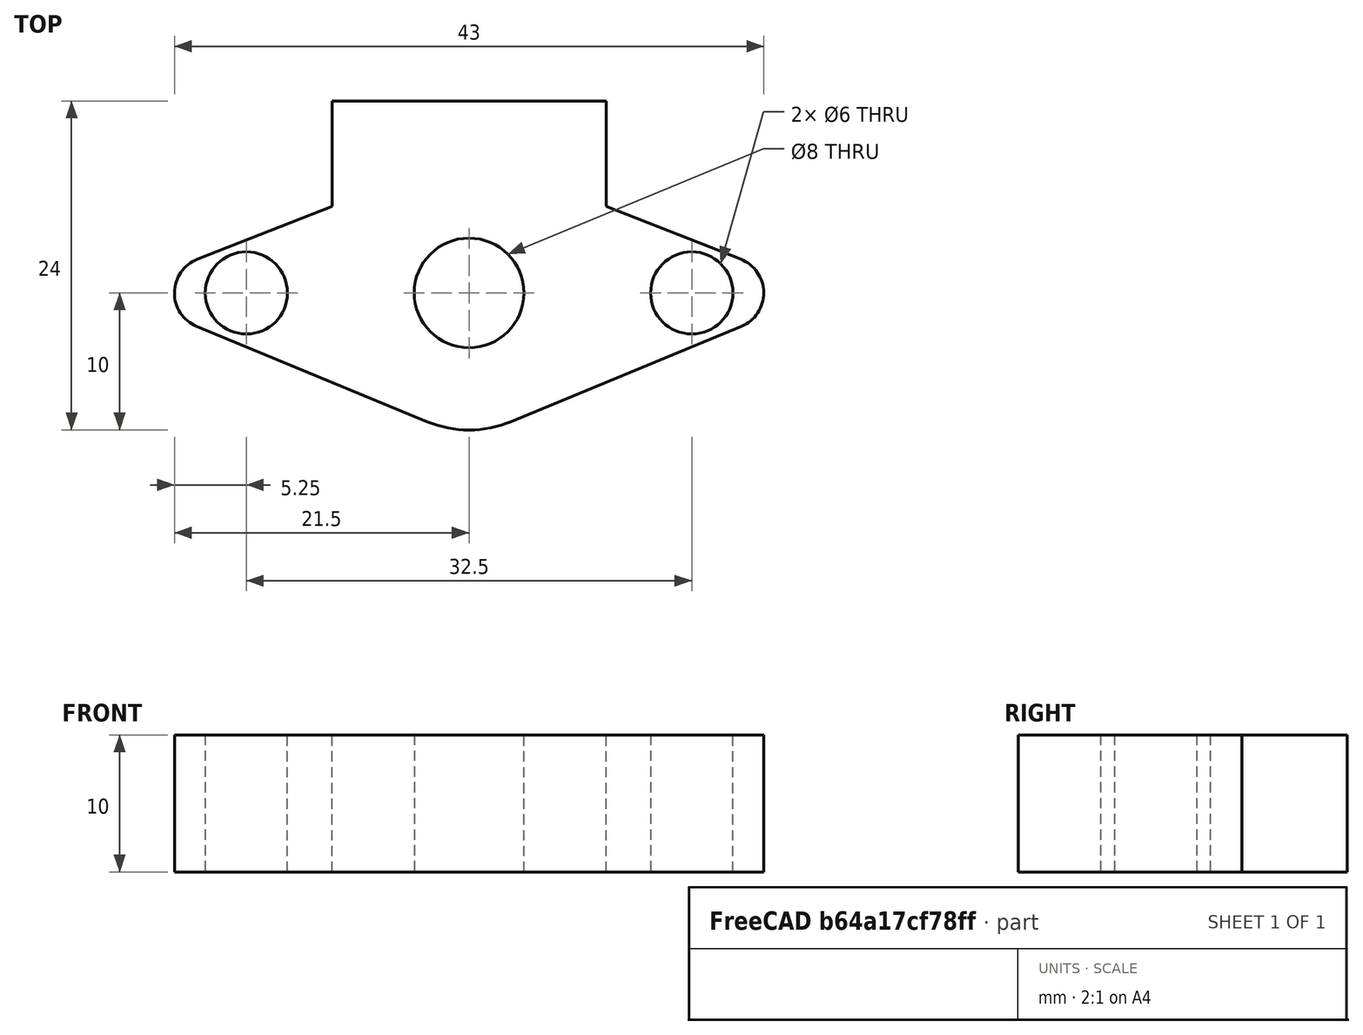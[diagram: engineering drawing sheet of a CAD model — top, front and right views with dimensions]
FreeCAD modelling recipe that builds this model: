
FCSTD DOCUMENT  (FreeCAD 0.16R6706 (Git))
Label: Suporte horizontal haste 8mm
License: All rights reserved
LicenseURL: http://en.wikipedia.org/wiki/All_rights_reserved
objects: Drawing::FeatureViewPython×5, Drawing::FeatureViewPart×2, Sketcher::SketchObject×1, PartDesign::Pad×1, Drawing::FeaturePage×1
note: 3 computed .brp shape members not serialized (recipe doc carries the construction recipe); baked Part::Feature solids carry a one-line shape summary decoded from their .brp

FEATURE [Sketcher::SketchObject] Sketch
  sketch-geometry (15):
    g0: LineSegment [constr] StartX=0 StartY=10 StartZ=0 EndX=0 EndY=-10 EndZ=0
    g1: LineSegment [constr] StartX=-21.5 StartY=0 StartZ=0 EndX=21.5 EndY=0 EndZ=0
    g2: LineSegment StartX=-19.8183 StartY=2.46551 StartZ=0 EndX=-10 EndY=6.31403 EndZ=0
    g3: LineSegment StartX=10 StartY=6.31403 StartZ=0 EndX=19.8183 EndY=2.46551 EndZ=0
    g4: LineSegment StartX=19.8633 StartY=-2.44736 StartZ=0 EndX=3.0585 EndY=-9.39286 EndZ=0
    g5: LineSegment StartX=-3.0585 StartY=-9.39286 StartZ=0 EndX=-19.8633 EndY=-2.44736 EndZ=0
    g6: ArcOfCircle CenterX=-18.8518 CenterY=0 CenterZ=0 NormalX=0 NormalY=0 NormalZ=1 Radius=2.64815 StartAngle=1.94437 EndAngle=4.32047
    g7: ArcOfCircle CenterX=18.8518 CenterY=0 CenterZ=0 NormalX=0 NormalY=0 NormalZ=1 Radius=2.64815 StartAngle=5.10431 EndAngle=7.48041
    g8: ArcOfCircle CenterX=0 CenterY=-1.99273 CenterZ=0 NormalX=0 NormalY=0 NormalZ=1 Radius=8.00727 StartAngle=4.32047 EndAngle=5.10431
    g9: Circle CenterX=0 CenterY=0 CenterZ=0 NormalX=0 NormalY=0 NormalZ=1 Radius=4
    g10: Circle CenterX=-16.25 CenterY=0 CenterZ=0 NormalX=0 NormalY=0 NormalZ=1 Radius=3
    g11: Circle CenterX=16.25 CenterY=0 CenterZ=0 NormalX=0 NormalY=0 NormalZ=1 Radius=3
    g12: LineSegment StartX=-10 StartY=14 StartZ=0 EndX=10 EndY=14 EndZ=0
    g13: LineSegment StartX=10 StartY=14 StartZ=0 EndX=10 EndY=6.31403 EndZ=0
    g14: LineSegment StartX=-10 StartY=6.31403 StartZ=0 EndX=-10 EndY=14 EndZ=0
  constraints (36):
    c: Vertical(g0)
    c: Horizontal(g1)
    c: Symmetric(g0,g0,g-1)
    c: Symmetric(g1,g1,g-1)
    c: Tangent(g2,g6) = 1.5708
    c: Tangent(g5,g6) = 1.5708
    c: Tangent(g3,g7) = 1.5708
    c: Tangent(g4,g7) = 1.5708
    c: Tangent(g4,g8) = 1.5708
    c: Tangent(g5,g8) = 1.5708
    c: PointOnObject(g7,g1)
    c: PointOnObject(g8,g0)
    c: PointOnObject(g6,g1)
    c: PointOnObject(g1,g6)
    c: PointOnObject(g1,g7)
    c: PointOnObject(g0,g8)
    c: DistanceY(g0,g0) = 20
    c: DistanceX(g1,g1) = 43
    c: Equal(g6,g7)
    c: PointOnObject(g11,g1)
    c: PointOnObject(g10,g1)
    c: Symmetric(g10,g11,g-1)
    c: Radius(g10) = 3
    c: Equal(g10,g11)
    c: Coincident(g9,g-1)
    c: Radius(g9) = 4
    c: DistanceX(g10,g11) = 32.5
    c: Coincident(g12,g13)
    c: Coincident(g14,g12)
    c: Horizontal(g12)
    c: Vertical(g13)
    c: Vertical(g14)
    c: Symmetric(g12,g12,g-2)
    c: DistanceX(g12,g12) = 20
    c: Coincident(g3,g13)
    c: Coincident(g2,g14)
FEATURE [PartDesign::Pad] Pad
  Length = 10
  Length2 = 100
  Sketch = -> Sketch
  Type = 0
FEATURE [Drawing::FeatureViewPart] Ortho  label="Ortho_0_0"
  Direction = (1,0,0)
  HiddenWidth = 0.15
  LineWidth = 0.35
  Rotation = -90
  Scale = 4
  ShowHiddenLines = true
  ShowSmoothLines = false
  Source = -> Pad
  Tolerance = 0.05
  ViewResult = <blob: 7028 chars omitted>
  Visible = true
  X = 97
  Y = 268.613
FEATURE [Drawing::FeatureViewPart] Ortho004  label="Ortho_0_1"
  Direction = (0,0,1)
  HiddenWidth = 0.15
  LineWidth = 0.35
  Rotation = 90
  Scale = 4
  ShowHiddenLines = true
  ShowSmoothLines = false
  Source = -> Pad
  Tolerance = 0.05
  ViewResult = <g id="Ortho_0_1"\n   transform="rotate(90,97,114.307) translate(97,114.307) scale(4,4)"\n  >\n<g   stroke="rgb(0, 0, 0)"\n   stroke-width="0.0375"\n   stroke-linecap="butt"\n   stroke-linejoin="miter"\n   stroke-dasharray="0.2,0.1"\n   fill="none"\n   transform="scale(1,-1)"\n  >\n<path id= "1" d=" M -3.0585 -9.39286 L -19.8633 -2.44736 " />\n<path d="M-19.8183 2.46551 A2.64815 2.64815 0 0 1 -19.8633 -2.44736" /><path id= "3" d=" M -19.8183 2.46551 L -10 6.31403 " />\n<path id= "4" d=" M -10 6.31403 L -10 14 " />\n<path id= "5" d=" M -10 14 L 10 14 " />\n<path id= "6" d=" M 10 14 L 10 6.31403 " />\n<path id= "7" d=" M 10 6.31403 L 19.8183 2.46551 " />\n<path d="M19.8633 -2.44736 A2.64815 2.64815 0 0 1 19.8183 2.46551" /><path id= "9" d=" M 19.8633 -2.44736 L 3.0585 -9.39286 " />\n<path d="M-3.0585 -9.39286 A8.00727 8.00727 0 0 1 3.0585 -9.39286" /><circle cx ="0" cy ="0" r ="4" /><circle cx ="16.25" cy ="0" r ="3" /><circle cx ="-16.25" cy ="0" r ="3" /></g>\n<g   stroke="rgb(0, 0, 0)"\n   stroke-width="0.0875"\n   stroke-linecap="butt"\n   stroke-linejoin="miter"\n   fill="none"\n   transform="scale(1,-1)"\n  >\n<path id= "1" d=" M -3.0585 -9.39286 L -19.8633 -2.44736 " />\n<path d="M-19.8183 2.46551 A2.64815 2.64815 0 0 1 -19.8633 -2.44736" /><path id= "3" d=" M -19.8183 2.46551 L -10 6.31403 " />\n<path id= "4" d=" M -10 6.31403 L -10 14 " />\n<path id= "5" d=" M -10 14 L 10 14 " />\n<path id= "6" d=" M 10 14 L 10 6.31403 " />\n<path id= "7" d=" M 10 6.31403 L 19.8183 2.46551 " />\n<path d="M19.8633 -2.44736 A2.64815 2.64815 0 0 1 19.8183 2.46551" /><path id= "9" d=" M 19.8633 -2.44736 L 3.0585 -9.39286 " />\n<path d="M-3.0585 -9.39286 A8.00727 8.00727 0 0 1 3.0585 -9.39286" /><circle cx ="0" cy ="0" r ="4" /><circle cx ="16.25" cy ="0" r ="3" /><circle cx ="-16.25" cy ="0" r ="3" /></g>\n</g>
  Visible = true
  X = 97
  Y = 114.307
FEATURE [Drawing::FeatureViewPython] dia001  # drawing view (typed FeaturePython)
  Rotation = 0
  ViewResult = <g>  <circle cx ="97.000000" cy ="49.307000" r="0.250000" stroke="none" fill="rgb(0,0,255)" /> \n<line x1="64.302913" y1="28.731089" x2="107.156354" y2="55.698280" style="stroke:rgb(0,0,255);stroke-width:0.50" />\n<polygon points="86.843646,42.915720 88.850127,45.359903 90.229097,45.046146 89.915341,43.667177" style="fill:rgb(0,0,255);stroke:rgb(0,0,255);stroke-width:0" />\n<polygon points="107.156354,55.698280 105.149873,53.254097 103.770903,53.567854 104.084659,54.946823" style="fill:rgb(0,0,255);stroke:rgb(0,0,255);stroke-width:0" />\n<line x1="64.302913" y1="28.731089" x2="43.096634" y2="28.731089" style="stroke:rgb(0,0,255);stroke-width:0.50" />\n<text x="53.699773" y="26.731089" font-family="inherit" font-size="3.6" fill="rgb(0,0,255)" text-anchor="middle" transform="rotate(0.000000 53.699773,26.731089)" >Ø6</text> </g>
  Visible = true
  X = 0
  Y = 0
  arrowL1 = 3
  arrowL2 = 1
  arrowW = 2
  arrow_scheme = 0
  autoPlaceOffset = 2
  autoPlaceText = true
  centerPointDia = 0.5
  click1_x = 64.3029
  click1_y = 28.7311
  click2_x = 43.0966
  click2_y = 27.3629
  click3_x = 43.0966
  click3_y = 27.3629
  comma_decimal_place = false
  lineColor = rgb(0,0,255)
  strokeWidth = 0.5
  textFormat_circular = Ø%(value)3.3f
  textRenderer_color = rgb(0,0,255)
  textRenderer_family = inherit
  textRenderer_size = 3.6
  unit_custom_scale = 1
  unit_scheme = 0
FEATURE [Drawing::FeatureViewPython] dia002  # drawing view (typed FeaturePython)
  Rotation = 0
  ViewResult = <g>  <circle cx ="97.000000" cy ="114.307000" r="0.250000" stroke="none" fill="rgb(0,0,255)" /> \n<line x1="51.989590" y1="73.537906" x2="108.858621" y2="125.048187" style="stroke:rgb(0,0,255);stroke-width:0.50" />\n<polygon points="85.141379,103.565813 86.693546,106.320949 88.106034,106.251110 88.036194,104.838622" style="fill:rgb(0,0,255);stroke:rgb(0,0,255);stroke-width:0" />\n<polygon points="108.858621,125.048187 107.306454,122.293051 105.893966,122.362890 105.963806,123.775378" style="fill:rgb(0,0,255);stroke:rgb(0,0,255);stroke-width:0" />\n<line x1="51.989590" y1="73.537906" x2="23.942574" y2="73.537906" style="stroke:rgb(0,0,255);stroke-width:0.50" />\n<text x="37.966082" y="71.537906" font-family="inherit" font-size="3.6" fill="rgb(0,0,255)" text-anchor="middle" transform="rotate(0.000000 37.966082,71.537906)" >Ø8</text> </g>
  Visible = true
  X = 0
  Y = 0
  arrowL1 = 3
  arrowL2 = 1
  arrowW = 2
  arrow_scheme = 0
  autoPlaceOffset = 2
  autoPlaceText = true
  centerPointDia = 0.5
  click1_x = 51.9896
  click1_y = 73.5379
  click2_x = 23.9426
  click2_y = 74.222
  click3_x = 23.9426
  click3_y = 74.222
  comma_decimal_place = false
  lineColor = rgb(0,0,255)
  strokeWidth = 0.5
  textFormat_circular = Ø%(value)3.3f
  textRenderer_color = rgb(0,0,255)
  textRenderer_family = inherit
  textRenderer_size = 3.6
  unit_custom_scale = 1
  unit_scheme = 0
FEATURE [Drawing::FeatureViewPython] dim001  # drawing view (typed FeaturePython)
  Rotation = 0
  ViewResult = <g> \n  <line x1="99.000000" y1="49.307000" x2="173.386534" y2="49.307000" style="stroke:rgb(0,0,255);stroke-width:0.50" />\n<line x1="99.000000" y1="179.307000" x2="173.386534" y2="179.307000" style="stroke:rgb(0,0,255);stroke-width:0.50" />\n<line x1="172.386534" y1="49.307000" x2="172.386534" y2="179.307000" style="stroke:rgb(0,0,255);stroke-width:0.50" /> \n  <polygon points="172.386534,179.307000 173.386534,176.307000 172.386534,175.307000 171.386534,176.307000" style="fill:rgb(0,0,255);stroke:rgb(0,0,255);stroke-width:0" /><polygon points="172.386534,49.307000 171.386534,52.307000 172.386534,53.307000 173.386534,52.307000" style="fill:rgb(0,0,255);stroke:rgb(0,0,255);stroke-width:0" /> \n  <text x="170.386534" y="114.307000" font-family="inherit" font-size="3.6" fill="rgb(0,0,255)" text-anchor="middle" transform="rotate(-90.000000 170.386534,114.307000)" >32.5</text> </g>
  Visible = true
  X = 0
  Y = 0
  arrowL1 = 3
  arrowL2 = 1
  arrowW = 2
  arrow_scheme = 0
  autoPlaceOffset = 2
  autoPlaceText = true
  click1_x = 172.387
  click1_y = 168.624
  click2_x = 172.387
  click2_y = 168.624
  comma_decimal_place = false
  dimension_line_overshoot = 1
  gap_datum_points = 2
  halfDimension_linear = false
  lineColor = rgb(0,0,255)
  strokeWidth = 0.5
  textFormat_linear = %(value)3.3f
  textRenderer_color = rgb(0,0,255)
  textRenderer_family = inherit
  textRenderer_size = 3.6
  unit_custom_scale = 1
  unit_scheme = 0
FEATURE [Drawing::FeatureViewPython] dim002  # drawing view (typed FeaturePython)
  Rotation = 0
  ViewResult = <g> \n  <line x1="155.000000" y1="228.613000" x2="188.778189" y2="228.613000" style="stroke:rgb(0,0,255);stroke-width:0.50" />\n<line x1="155.000000" y1="268.613000" x2="188.778189" y2="268.613000" style="stroke:rgb(0,0,255);stroke-width:0.50" />\n<line x1="187.778189" y1="228.613000" x2="187.778189" y2="268.613000" style="stroke:rgb(0,0,255);stroke-width:0.50" /> \n  <polygon points="187.778189,268.613000 188.778189,265.613000 187.778189,264.613000 186.778189,265.613000" style="fill:rgb(0,0,255);stroke:rgb(0,0,255);stroke-width:0" /><polygon points="187.778189,228.613000 186.778189,231.613000 187.778189,232.613000 188.778189,231.613000" style="fill:rgb(0,0,255);stroke:rgb(0,0,255);stroke-width:0" /> \n  <text x="185.778189" y="248.613000" font-family="inherit" font-size="3.6" fill="rgb(0,0,255)" text-anchor="middle" transform="rotate(-90.000000 185.778189,248.613000)" >10</text> </g>
  Visible = true
  X = 0
  Y = 0
  arrowL1 = 3
  arrowL2 = 1
  arrowW = 2
  arrow_scheme = 0
  autoPlaceOffset = 2
  autoPlaceText = true
  click1_x = 187.778
  click1_y = 263.71
  click2_x = 187.778
  click2_y = 263.71
  comma_decimal_place = false
  dimension_line_overshoot = 1
  gap_datum_points = 2
  halfDimension_linear = false
  lineColor = rgb(0,0,255)
  strokeWidth = 0.5
  textFormat_linear = %(value)3.3f
  textRenderer_color = rgb(0,0,255)
  textRenderer_family = inherit
  textRenderer_size = 3.6
  unit_custom_scale = 1
  unit_scheme = 0
FEATURE [Drawing::FeatureViewPython] dim003  # drawing view (typed FeaturePython)
  Rotation = 0
  ViewResult = <g> \n  <line x1="97.000000" y1="116.307000" x2="97.000000" y2="209.984469" style="stroke:rgb(0,0,255);stroke-width:0.50" />\n<line x1="59.428560" y1="128.541000" x2="59.428560" y2="209.984469" style="stroke:rgb(0,0,255);stroke-width:0.50" />\n<line x1="97.000000" y1="208.984469" x2="59.428560" y2="208.984469" style="stroke:rgb(0,0,255);stroke-width:0.50" /> \n  <polygon points="59.428560,208.984469 62.428560,209.984469 63.428560,208.984469 62.428560,207.984469" style="fill:rgb(0,0,255);stroke:rgb(0,0,255);stroke-width:0" /><polygon points="97.000000,208.984469 94.000000,207.984469 93.000000,208.984469 94.000000,209.984469" style="fill:rgb(0,0,255);stroke:rgb(0,0,255);stroke-width:0" /> \n  <text x="78.214280" y="206.984469" font-family="inherit" font-size="3.6" fill="rgb(0,0,255)" text-anchor="middle" transform="rotate(0.000000 78.214280,206.984469)" >10</text> </g>
  Visible = true
  X = 0
  Y = 0
  arrowL1 = 3
  arrowL2 = 1
  arrowW = 2
  arrow_scheme = 0
  autoPlaceOffset = 2
  autoPlaceText = true
  click1_x = 68.0653
  click1_y = 208.984
  click2_x = 68.0653
  click2_y = 208.984
  comma_decimal_place = false
  dimension_line_overshoot = 1
  gap_datum_points = 2
  halfDimension_linear = false
  lineColor = rgb(0,0,255)
  strokeWidth = 0.5
  textFormat_linear = 10
  textRenderer_color = rgb(0,0,255)
  textRenderer_family = inherit
  textRenderer_size = 3.6
  unit_custom_scale = 1
  unit_scheme = 0
FEATURE [Drawing::FeaturePage] Page
  Group = -> [Ortho,Ortho004,dia001,dia002,dim001,dim002,dim003]
